# Revit family: M_Downlight - Recessed Can
name_source: partatom
category: Lighting Fixtures
revit_build: Autodesk Revit 2017 (Build: 20160109_1515(x64)
units: mm (PartAtom-declared; Revit-internal decimal feet)

## family parameters
Always vertical = No
Cut with Voids When Loaded = No
Host = Ceiling
Light Source = Yes
OmniClass Number = 23.80.70.11.14.11
OmniClass Title = Downlights
Part Type = Normal
Room Calculation Point = No
Round Connector Dimension = Use Diameter
Shared = No

## types (6) — shared parameters
Ballast Number of Poles = 1
Color Filter = 16777215
Diffuser = Glass, White, High Luminance
Dimming Lamp Color Temperature Shift = <None>
Load Classification = Lighting - Dwelling Unit
Recessing Height = 200 mm  [stored 0.656168 ft]
Shade = Steel, Paint Finish, Dark Gray, Matte
Spot Beam Angle = 30.00°
Spot Field Angle = 90.00°
Tilt Angle = 90.00°

## per-type parameters (varying)
| type | Apparent Load | Assembly Code | Ballast Voltage | Lamp | Light Source Symbol Length | Recessing Diameter | Recessing Inner Radius | Recessing Radius |
| 152mm Incandescent - 120V | 60 VA | D5020220 | 120 V | A-19 | 3048 mm  [stored 10 ft] | 150 mm | 62 mm | 75 mm |
| 203mm Incandescent - 120V | 100 VA | D5020220 | 120 V | A-19 | 3048 mm  [stored 10 ft] | 200 mm  [stored 0.656168 ft] | 87 mm | 100 mm  [stored 0.328084 ft] |
| 152mm Incandescent - 277V | 60 VA | D5020220 | 277 V | A-19 | 3048 mm  [stored 10 ft] | 150 mm | 62 mm | 75 mm |
| 203mm Incandescent - 277V | 100 VA | D5020220 | 277 V | A-19 | 3048 mm  [stored 10 ft] | 200 mm  [stored 0.656168 ft] | 87 mm | 100 mm  [stored 0.328084 ft] |
| Fluorescent - 120V | 18 VA | D5020210 | 120 V |  | 3048 mm  [stored 10 ft] | 200 mm  [stored 0.656168 ft] | 87 mm | 100 mm  [stored 0.328084 ft] |
| Fluorescent - 277V | 18 VA | D5020210 | 277 V |  | 1500 mm  [stored 4.92126 ft] | 200 mm  [stored 0.656168 ft] | 87 mm | 100 mm  [stored 0.328084 ft] |

note: [stored X ft] marks values corroborated as IEEE doubles in the binary element streams (Revit-internal decimal feet)

## geometry (parser evidence)
native form markers: Blend x4, Sweep x1
no freeform markers — native parametric forms only
